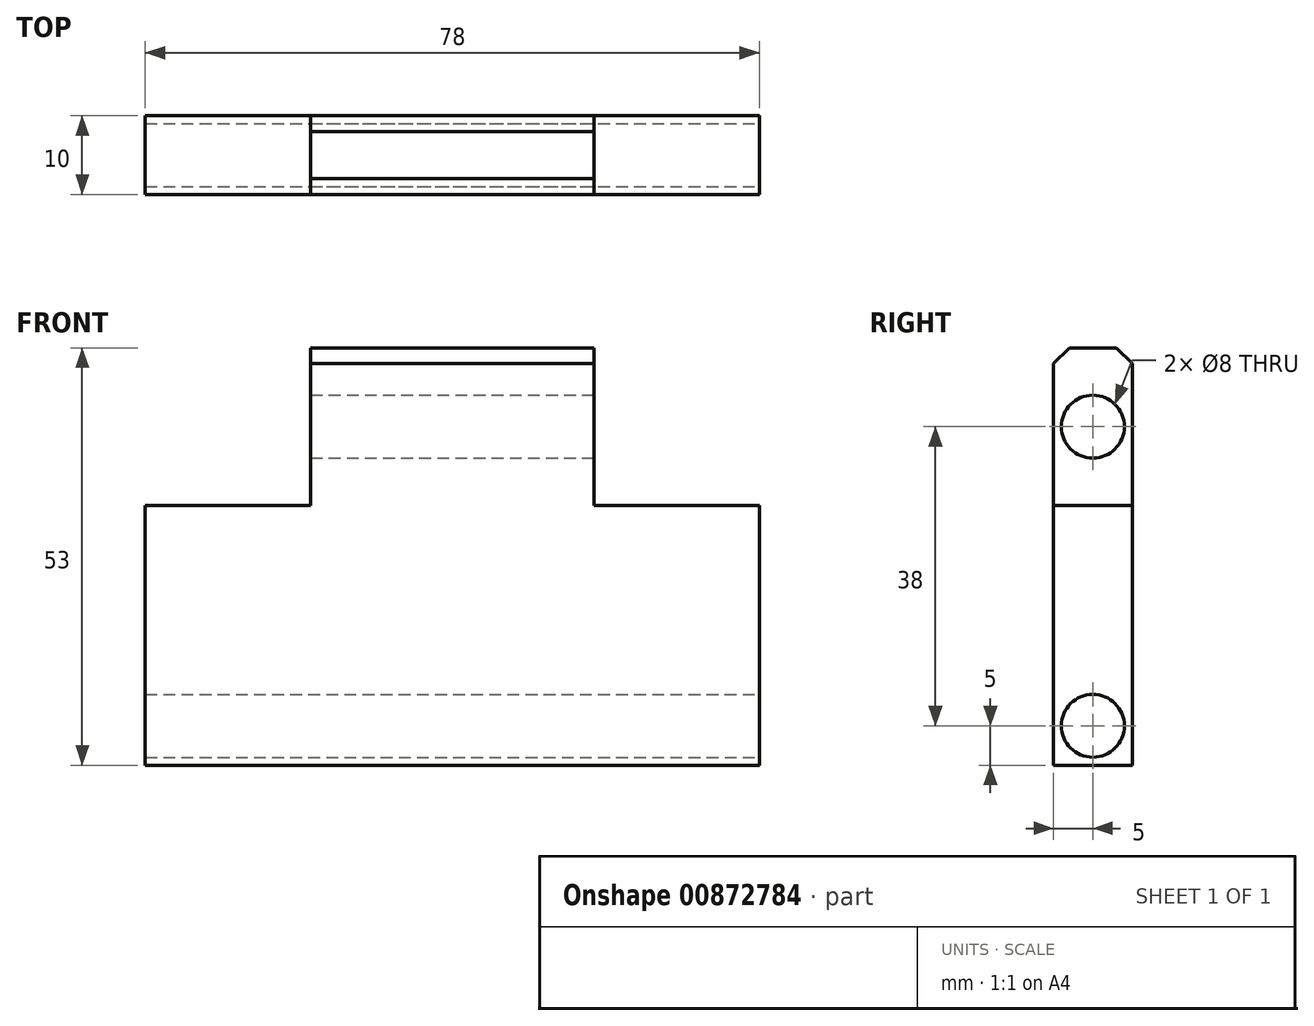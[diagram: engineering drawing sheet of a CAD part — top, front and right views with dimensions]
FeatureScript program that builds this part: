
annotation { "Feature Type Name" : "Feature", "Feature Type Description" : "" }
export const myFeature = defineFeature(function(context is Context, id is Id, definition is map)
    precondition{}
    {
        {
            var Q0;
            Q0=qCreatedBy(makeId("Front.planeOp"),FACE);
            var sketch = newSketch(context, id + "F0", { "sketchPlane" : qUnion([Q0])});
            skLineSegment(sketch, "E0.bottom", {"start": v(-19, 24) * mm, "end": v(19, 24) * mm});
            skLineSegment(sketch, "E0.top", {"start": v(-35, -24) * mm, "end": v(35, -24) * mm});
            skLineSegment(sketch, "E0.left", {"start": v(-35, 9) * mm, "end": v(-35, -24) * mm});
            skLineSegment(sketch, "E0.right", {"start": v(35, 9) * mm, "end": v(35, -24) * mm});
            skPoint(sketch, "E0.middle", {"position": v(0, 0) * mm});
            skLineSegment(sketch, "E1.left", {"start": v(19, 9) * mm, "end": v(19, 24) * mm});
            skLineSegment(sketch, "E1.right", {"start": v(-19, 9) * mm, "end": v(-19, 24) * mm});
            skPoint(sketch, "E1.middle", {"position": v(0, 24) * mm});
            skLineSegment(sketch, "E2", {"start": v(-19, 9) * mm, "end": v(-35, 9) * mm});
            skLineSegment(sketch, "E3", {"start": v(-35, 9) * mm, "end": v(-19, 9) * mm});
            skPoint(sketch, "E4.orphan", {"position": v(-35, 24) * mm});
            skLineSegment(sketch, "E5", {"start": v(19, 9) * mm, "end": v(35, 9) * mm});
            skPoint(sketch, "E6.orphan", {"position": v(35, 24) * mm});
            skSolve(sketch);
        }
        {
            var Q0;
            Q0=makeQuery(id+"F0.imprint","IMPRINT",FACE,{"disambiguationData":[TD([[makeQuery(id+"F0.imprint","IMPRINT",EDGE,{"derivedFrom":sQuery(id+"F0.wireOp",EDGE,"E0.bottom")}),-1.0]])]});
            extrude(context, id + "F1", {"entities" : qUnion([Q0]), "depth" : 10 * mm, "offsetDistance" : 25 * mm});
        }
        {
            var Q0;
            Q0=makeQuery(id+"F1.opExtrude","SWEPT_FACE",FACE,{"disambiguationData":[OSD([sQuery(id+"F0.wireOp",EDGE,"E1.left")])]});
            var sketch = newSketch(context, id + "F2", { "sketchPlane" : qUnion([Q0])});
            skCircle(sketch, "E7", {"center": v(-5, 19) * mm, "radius": 4 * mm});
            skPoint(sketch, "E7.centerSnap0", {"position": v(-5, 24) * mm});
            skSolve(sketch);
        }
        {
            var Q0;
            Q0=qSketchRegion(id+"F2",true);
            extrude(context, id + "F3", {"entities" : qUnion([Q0]), "operationType" : NewBodyOperationType.REMOVE, "oppositeDirection" : true, "depth" : 38 * mm, "offsetDistance" : 25 * mm});
        }
        {
            var Q0;
            Q0=makeQuery(id+"F1.opExtrude","SWEPT_FACE",FACE,{"disambiguationData":[OSD([sQuery(id+"F0.wireOp",EDGE,"E0.right")])]});
            var sketch = newSketch(context, id + "F4", { "sketchPlane" : qUnion([Q0])});
            skCircle(sketch, "E8", {"center": v(-5, -19) * mm, "radius": 4 * mm});
            skPoint(sketch, "E8.centerSnap0", {"position": v(-5, -24) * mm});
            skSolve(sketch);
        }
        {
            var Q0;
            Q0=makeQuery(id+"F4.imprint","IMPRINT",FACE,{"disambiguationData":[TD([[makeQuery(id+"F4.imprint","IMPRINT",EDGE,{"derivedFrom":sQuery(id+"F4.wireOp",EDGE,"E8")}),1.0]])]});
            extrude(context, id + "F5", {"entities" : qUnion([Q0]), "operationType" : NewBodyOperationType.REMOVE, "oppositeDirection" : true, "depth" : 70 * mm, "offsetDistance" : 25 * mm});
        }
        {
            var Q0;
            Q0=makeQuery(id+"F1.opExtrude","SWEPT_BODY",BODY,{"disambiguationData":[OSD([sQuery(id+"F0.wireOp",EDGE,"E0.bottom"),sQuery(id+"F0.wireOp",EDGE,"E0.top"),sQuery(id+"F0.wireOp",EDGE,"E0.left"),sQuery(id+"F0.wireOp",EDGE,"E0.right"),sQuery(id+"F0.wireOp",EDGE,"E1.left"),sQuery(id+"F0.wireOp",EDGE,"E1.right"),sQuery(id+"F0.wireOp",EDGE,"E3"),sQuery(id+"F0.wireOp",EDGE,"E5")])]});
            deleteBodies(context, id + "F6", {"entities" : qUnion([Q0])});
        }
        {
            var Q0;
            Q0=qCreatedBy(makeId("Front.planeOp"),FACE);
            var sketch = newSketch(context, id + "F7", { "sketchPlane" : qUnion([Q0])});
            skLineSegment(sketch, "E9.bottom", {"start": v(-18, 24) * mm, "end": v(18, 24) * mm});
            skLineSegment(sketch, "E9.top", {"start": v(-39, -24) * mm, "end": v(39, -24) * mm});
            skLineSegment(sketch, "E9.left", {"start": v(-39, 9) * mm, "end": v(-39, -24) * mm});
            skLineSegment(sketch, "E9.right", {"start": v(39, 9) * mm, "end": v(39, -24) * mm});
            skPoint(sketch, "E9.middle", {"position": v(0, 0) * mm});
            skLineSegment(sketch, "E10.top", {"start": v(-39, 9) * mm, "end": v(-18, 9) * mm});
            skLineSegment(sketch, "E10.right", {"start": v(-18, 24) * mm, "end": v(-18, 9) * mm});
            skLineSegment(sketch, "E11.top", {"start": v(39, 9) * mm, "end": v(18, 9) * mm});
            skLineSegment(sketch, "E11.right", {"start": v(18, 24) * mm, "end": v(18, 9) * mm});
            skSolve(sketch);
        }
        {
            var Q0;
            Q0=qSketchRegion(id+"F7",true);
            var Q1;
            Q1=makeQuery(id+"F7.imprint","IMPRINT",FACE,{"disambiguationData":[TD([[makeQuery(id+"F7.imprint","IMPRINT",EDGE,{"derivedFrom":sQuery(id+"F7.wireOp",EDGE,"E9.bottom")}),-1.0]])]});
            extrude(context, id + "F8", {"entities" : qUnion([Q0, Q1]), "depth" : 10 * mm, "offsetDistance" : 25 * mm});
        }
        {
            var Q0;
            Q0=makeQuery(id+"F8.opExtrude","SWEPT_FACE",FACE,{"disambiguationData":[OSD([sQuery(id+"F7.wireOp",EDGE,"E11.right")])]});
            var sketch = newSketch(context, id + "F9", { "sketchPlane" : qUnion([Q0])});
            skCircle(sketch, "E12", {"center": v(-5, 19) * mm, "radius": 4 * mm});
            skPoint(sketch, "E12.centerSnap0", {"position": v(-5, 24) * mm});
            skSolve(sketch);
        }
        {
            var Q0;
            Q0=qSketchRegion(id+"F9",true);
            extrude(context, id + "F10", {"entities" : qUnion([Q0]), "operationType" : NewBodyOperationType.REMOVE, "oppositeDirection" : true, "depth" : 40 * mm, "offsetDistance" : 25 * mm});
        }
        {
            var Q0;
            Q0=makeQuery(id+"F8.opExtrude","SWEPT_FACE",FACE,{"disambiguationData":[OSD([sQuery(id+"F7.wireOp",EDGE,"E9.right")])]});
            var sketch = newSketch(context, id + "F11", { "sketchPlane" : qUnion([Q0])});
            skCircle(sketch, "E13", {"center": v(-5, -19) * mm, "radius": 4 * mm});
            skPoint(sketch, "E13.centerSnap0", {"position": v(-5, -24) * mm});
            skSolve(sketch);
        }
        {
            var Q0;
            Q0=qSketchRegion(id+"F11",true);
            extrude(context, id + "F12", {"entities" : qUnion([Q0]), "operationType" : NewBodyOperationType.REMOVE, "oppositeDirection" : true, "depth" : 100 * mm, "offsetDistance" : 25 * mm});
        }
        {
            var Q0;
            Q0=makeQuery(id+"F8.opExtrude","SWEPT_FACE",FACE,{"disambiguationData":[OSD([sQuery(id+"F7.wireOp",EDGE,"E9.bottom")])]});
            extrude(context, id + "F13", {"entities" : qUnion([Q0]), "operationType" : NewBodyOperationType.ADD, "depth" : 5 * mm, "offsetDistance" : 25 * mm});
        }
        {
            var Q0;
            {var subQ0=sQuery(id+"F7.wireOp",EDGE,"E9.bottom");Q0=makeQuery(id+"F13.opExtrude","CAP_EDGE",EDGE,{"disambiguationData":[OSD([subQ0]),TDD([makeQuery(id+"F8.opExtrude","CAP_EDGE",EDGE,{"disambiguationData":[OSD([subQ0])],"isStart":false})])],"isStart":false});}
            var Q1;
            {var subQ0=sQuery(id+"F7.wireOp",EDGE,"E9.bottom");Q1=makeQuery(id+"F13.opExtrude","CAP_EDGE",EDGE,{"disambiguationData":[OSD([subQ0]),TDD([makeQuery(id+"F8.opExtrude","CAP_EDGE",EDGE,{"disambiguationData":[OSD([subQ0])],"isStart":true})])],"isStart":false});}
            chamfer(context, id + "F14", {"entities" : qUnion([Q0, Q1]), "width" : 2 * mm, "tangentPropagation" : true});
        }
    });
